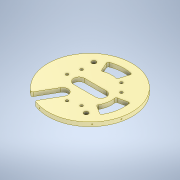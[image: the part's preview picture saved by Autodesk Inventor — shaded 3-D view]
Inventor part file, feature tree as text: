
AUTODESK INVENTOR PART (.ipt)
format: ipt  version: 2021 (Build 250183000, 183)  size: 380,416 bytes
history: native  units: in
note: dims shown in document units (in); Inventor stores cm internally (conversion verified against a paired STEP export)
features: other x14, extrude x5, hole x4, pattern_circular x3, fillet x1
ambient origin geometry x8: Origin, YZ Plane, XZ Plane, XY Plane, X Axis, Y Axis, Z Axis, Center Point
bodies: Solid1 (feature_tree)
feature tree (27):
  other  "End Cap"
  extrude  "Cylinders Cutout"  TaperAngle=0.0deg  [1 undecoded]
  extrude  "Wedges Cutout"  TaperAngle=0.0deg  [1 undecoded]
  extrude  "Rope Holes Cutout"  Depth=7.75in
  extrude  "Support Holes Cutout"  Depth=1.0in
  other  "Set Screw Sketch"
  other  "Edge Hole Plane 1"
  other  "Edge Hole Plane 2"
  other  "Edge Hole Center 1"
  other  "Edge Hole Center 2"
  other  "Central Plane"
  hole  "Insert Edge Hole 1"  [1 undecoded]
  hole  "Insert Edge Hole 2"  [1 undecoded]
  pattern_circular  "Circular Pattern2"  [2 undecoded]
  pattern_circular  "Circular Pattern3"  [2 undecoded]
  extrude  "Cutouts extrude"  Depth=2.0132in
  fillet  "Fillet1"  [1 undecoded]
  other  "Edge Hole Center 1 - Unthreaded"
  other  "Edge Hole Center 2 - Unthreaded"
  hole  "Edge Hole 1 - Unthreaded"  [1 undecoded]
  hole  "Edge Hole 2 - Unthreaded"  [1 undecoded]
  pattern_circular  "Circular Pattern4"  [2 undecoded]
  other  "Cylinders Sketch"
  other  "Wedges Sketch"
  other  "Rope Holes Sketch"
  other  "Support Holes Sketch"
  other  "Cutouts"
note: 13 required parameter values undecoded (feature->parameter linkage not recoverable at this tier; creation-order binding heuristic only, values carry confidence <= 0.55)
